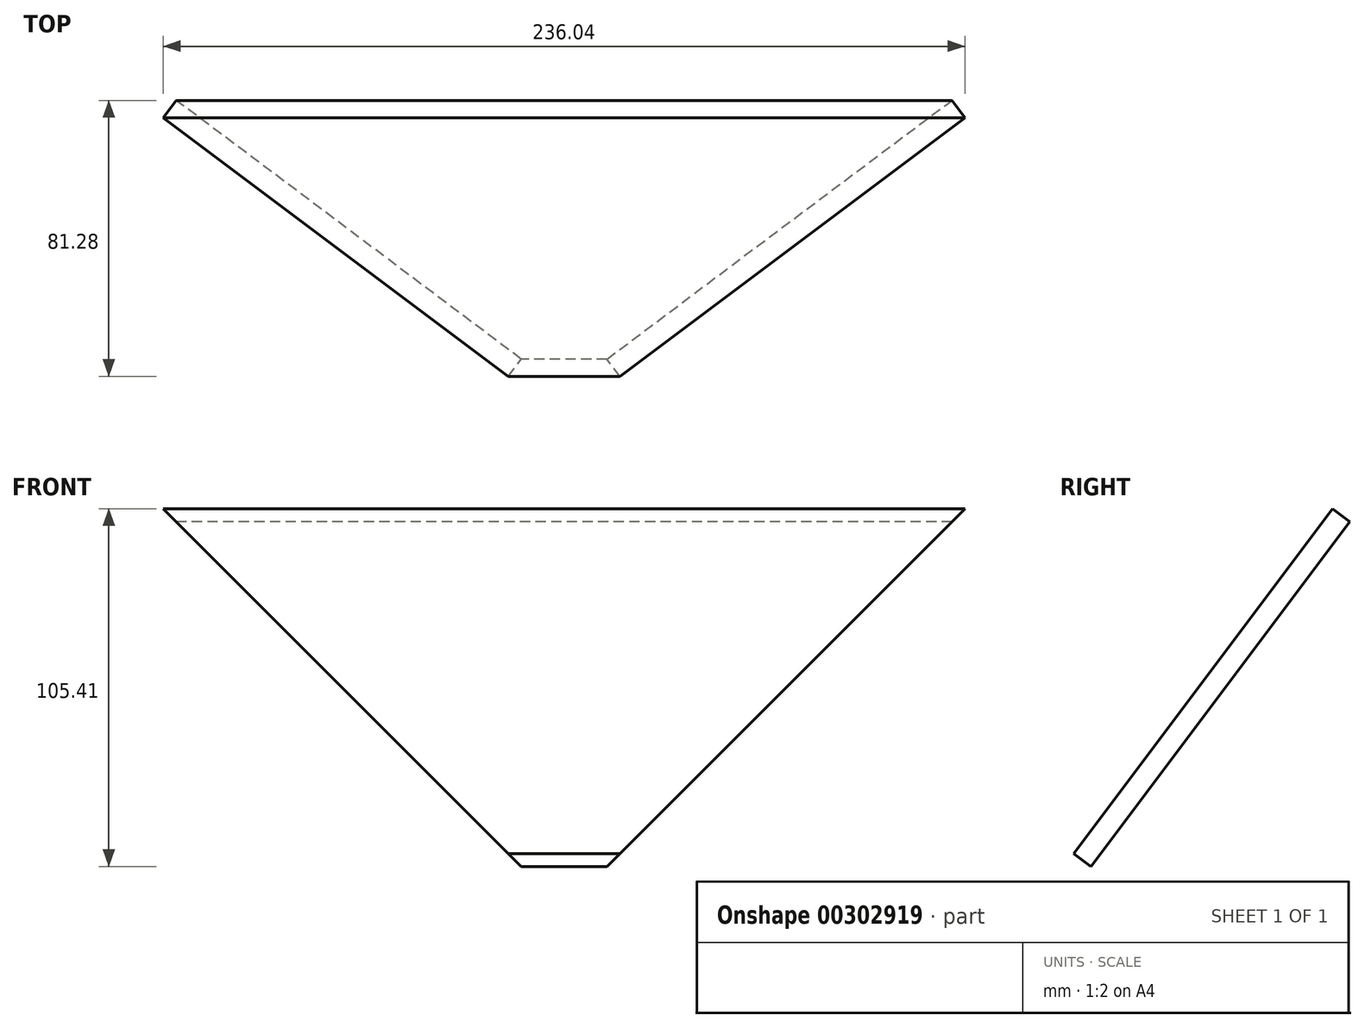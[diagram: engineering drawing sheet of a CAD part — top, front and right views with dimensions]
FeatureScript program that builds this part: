
annotation { "Feature Type Name" : "Feature", "Feature Type Description" : "" }
export const myFeature = defineFeature(function(context is Context, id is Id, definition is map)
    precondition{}
    {
        {
            var Q0;
            Q0=qCreatedBy(makeId("Right.planeOp"),FACE);
            var sketch = newSketch(context, id + "F0", { "sketchPlane" : qUnion([Q0])});
            skPoint(sketch, "E0.middle", {"position": v(0, 0) * mm});
            skLineSegment(sketch, "E1", {"start": v(0, 0) * mm, "end": v(-76.2, 0) * mm});
            skLineSegment(sketch, "E2", {"start": v(-76.2, 0) * mm, "end": v(0, 101.6) * mm});
            skLineSegment(sketch, "E3", {"start": v(0, 101.6) * mm, "end": v(0, 0) * mm});
            skLineSegment(sketch, "E4", {"start": v(0, 101.6) * mm, "end": v(-5.08, 105.4) * mm});
            skLineSegment(sketch, "E5", {"start": v(-5.08, 105.41) * mm, "end": v(-81.28, 3.8) * mm});
            skLineSegment(sketch, "E6", {"start": v(-81.28, 3.8) * mm, "end": v(-76.2, 0) * mm});
            skSolve(sketch);
        }
        {
            var Q0;
            Q0=makeQuery(id+"F0.imprint","IMPRINT",FACE,{"disambiguationData":[TD([[makeQuery(id+"F0.imprint","IMPRINT",EDGE,{"derivedFrom":sQuery(id+"F0.wireOp",EDGE,"E2")}),1.0]])]});
            extrude(context, id + "F1", {"entities" : qUnion([Q0]), "depth" : 241.3 * mm});
        }
        {
            var Q0;
            Q0=qCreatedBy(makeId("Front.planeOp"),FACE);
            var sketch = newSketch(context, id + "F2", { "sketchPlane" : qUnion([Q0])});
            skLineSegment(sketch, "E7.bottom", {"start": v(0, 0) * mm, "end": v(241.3, 0) * mm});
            skLineSegment(sketch, "E7.top", {"start": v(-5.4, 105.4) * mm, "end": v(241.3, 105.4) * mm});
            skLineSegment(sketch, "E7.left", {"start": v(0, 0) * mm, "end": v(0, 105.41) * mm});
            skLineSegment(sketch, "E7.right", {"start": v(241.3, 0) * mm, "end": v(241.3, 105.4) * mm});
            skLineSegment(sketch, "E8", {"start": v(236.04, 105.41) * mm, "end": v(130.63, 0) * mm});
            skLineSegment(sketch, "E9", {"start": v(0, 105.41) * mm, "end": v(105.41, 0) * mm});
            skSolve(sketch);
        }
        {
            var Q0;
            {var subQ0=sQuery(id+"F2.wireOp",EDGE,"E7.right");Q0=makeQuery(id+"F2.imprint","IMPRINT",FACE,{"disambiguationData":[TD([[makeQuery(id+"F2.imprint","IMPRINT",EDGE,{"derivedFrom":subQ0}),1.0]])]});}
            var Q1;
            {var subQ0=sQuery(id+"F2.wireOp",EDGE,"E7.left");Q1=makeQuery(id+"F2.imprint","IMPRINT",FACE,{"disambiguationData":[TD([[makeQuery(id+"F2.imprint","IMPRINT",EDGE,{"derivedFrom":subQ0}),-1.0]])]});}
            extrude(context, id + "F3", {"entities" : qUnion([Q0, Q1]), "operationType" : NewBodyOperationType.REMOVE, "endBound" : BoundingType.THROUGH_ALL, "depth" : 25.4 * mm});
        }
    });
